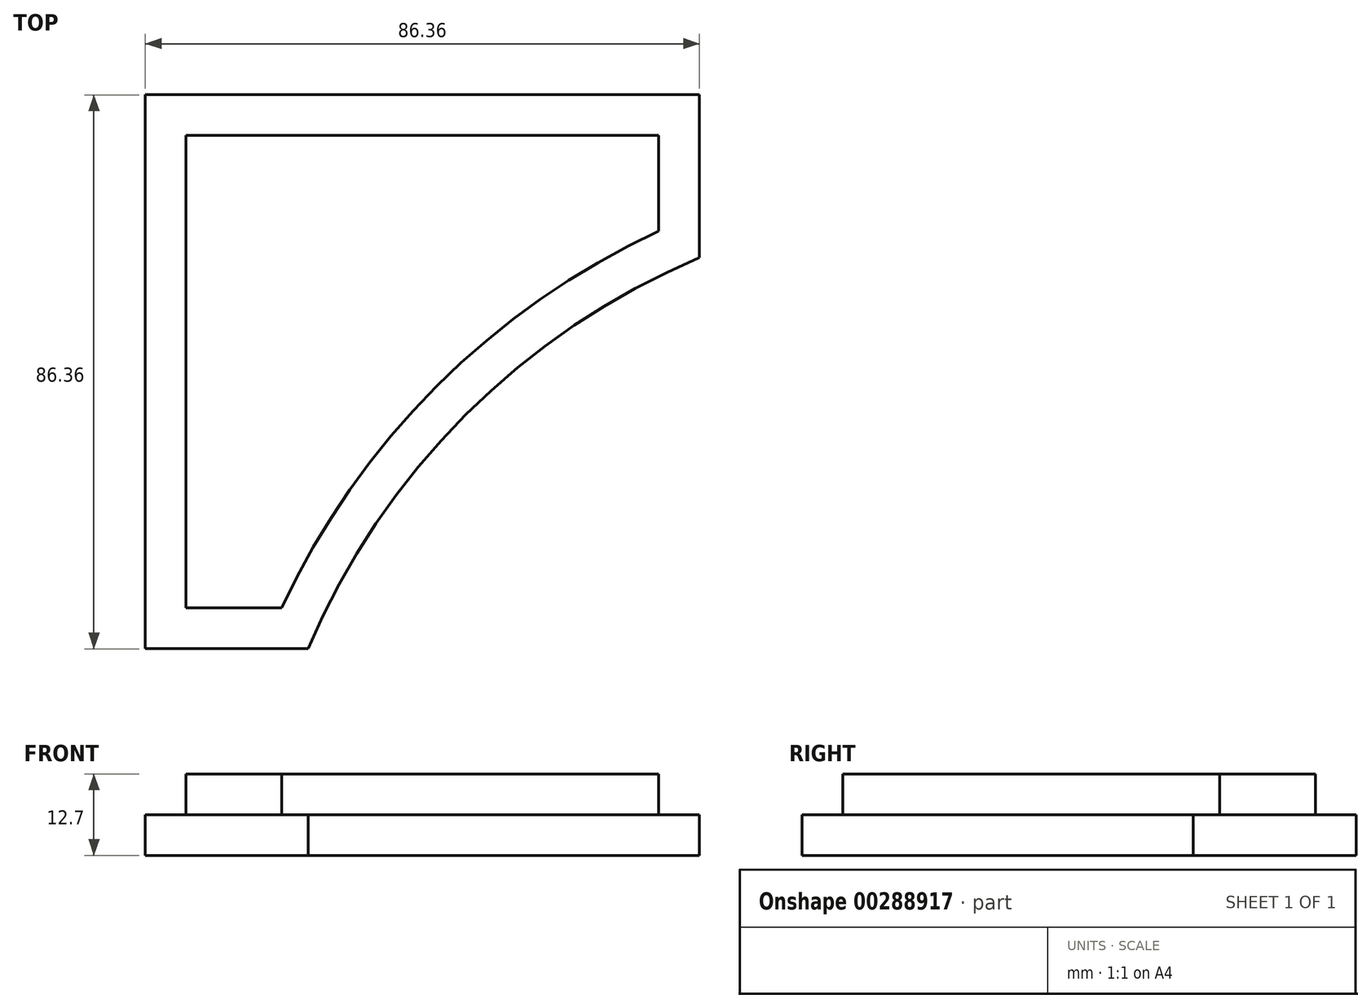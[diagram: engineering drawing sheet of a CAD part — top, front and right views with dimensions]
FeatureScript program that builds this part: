
annotation { "Feature Type Name" : "Feature", "Feature Type Description" : "" }
export const myFeature = defineFeature(function(context is Context, id is Id, definition is map)
    precondition{}
    {
        {
            var Q0;
            Q0=qCreatedBy(makeId("Top.planeOp"),FACE);
            var sketch = newSketch(context, id + "F0", { "sketchPlane" : qUnion([Q0])});
            skLineSegment(sketch, "E0.bottom", {"start": v(-130.73, 130.73) * mm, "end": v(-44.37, 130.73) * mm});
            skLineSegment(sketch, "E0.left", {"start": v(-130.73, 130.73) * mm, "end": v(-130.73, 44.37) * mm});
            skPoint(sketch, "E0.middle", {"position": v(0, 0) * mm});
            skLineSegment(sketch, "E1.bottom", {"start": v(-130.73, 44.37) * mm, "end": v(-105.33, 44.37) * mm});
            skLineSegment(sketch, "E2.left", {"start": v(-44.37, 130.73) * mm, "end": v(-44.37, 105.33) * mm});
            skArc(sketch, "E3", {"start": v(-44.37, 105.33) * mm, "mid": v(-80.82, 80.82) * mm, "end": v(-105.33, 44.37) * mm});
            skSolve(sketch);
        }
        {
            var Q0;
            Q0=qSketchRegion(id+"F0",true);
            extrude(context, id + "F1", {"entities" : qUnion([Q0]), "depth" : 12.7 * mm});
        }
        {
            var Q0;
            Q0=makeQuery(id+"F1.opExtrude","CAP_FACE",FACE,{"disambiguationData":[OSD([sQuery(id+"F0.wireOp",EDGE,"E0.bottom"),sQuery(id+"F0.wireOp",EDGE,"E0.left"),sQuery(id+"F0.wireOp",EDGE,"pLTumg3k-l0Sz-kjWU-tW42-cAAd8CBKG7LP"),sQuery(id+"F0.wireOp",EDGE,"E1.bottom"),sQuery(id+"F0.wireOp",EDGE,"E2.left")])],"isStart":false});
            var sketch = newSketch(context, id + "F2", { "sketchPlane" : qUnion([Q0])});
            skLineSegment(sketch, "E4.0", {"start": v(-50.72, 124.38) * mm, "end": v(-50.72, 109.47) * mm});
            skLineSegment(sketch, "E4.1", {"start": v(-124.38, 124.38) * mm, "end": v(-50.72, 124.38) * mm});
            skArc(sketch, "E4.2", {"start": v(-50.72, 109.47) * mm, "mid": v(-85.31, 85.31) * mm, "end": v(-109.47, 50.72) * mm});
            skLineSegment(sketch, "E4.3", {"start": v(-124.38, 50.72) * mm, "end": v(-109.47, 50.72) * mm});
            skLineSegment(sketch, "E4.4", {"start": v(-124.38, 124.38) * mm, "end": v(-124.38, 50.72) * mm});
            skSolve(sketch);
        }
        {
            var Q0;
            Q0=makeQuery(id+"F2.imprint","IMPRINT",FACE,{"disambiguationData":[TD([[makeQuery(id+"F2.imprint","IMPRINT",EDGE,{"derivedFrom":sQuery(id+"F2.wireOp",EDGE,"E4.0")}),1.0]])]});
            var Q1;
            Q1=qConstructionFilter(qBodyType(qCreatedBy(id+"F2",EDGE),BodyType.WIRE),ConstructionObject.NO);
            extrude(context, id + "F3", {"entities" : qUnion([Q0]), "operationType" : NewBodyOperationType.REMOVE, "surfaceEntities" : qUnion([Q1]), "oppositeDirection" : true, "depth" : 6.35 * mm});
        }
    });
